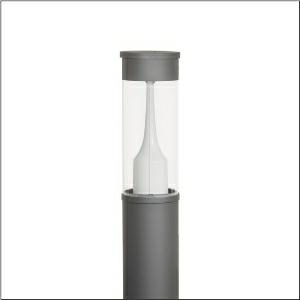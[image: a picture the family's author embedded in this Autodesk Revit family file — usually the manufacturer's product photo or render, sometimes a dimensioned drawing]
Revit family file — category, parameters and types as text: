
# Revit family: city-light_260_iq___st1_2a_5xa5295mf14h_84f0
name_source: partatom
category: Lighting Fixtures
units: mm (PartAtom-declared; Revit-internal decimal feet)

## family parameters
Cut with Voids When Loaded = No
Host = Face
Light Source = No
Part Type = Normal
Room Calculation Point = No
Round Connector Dimension = Use Diameter
Shared = No

## types (1)
- --- (1 x LED, 1540 lm, 11.8 W, 2700K)
    Apparent Load = 12 VA
    CIE Flux Codes = 22 61 93 96 100
    Color Rendering = 70
    Color Temperature = 2700K
    Default Elevation = 1800 mm
    Description = City-Light 260 iQ, light pillar, Module 540 iQ-SR, primary light control with 3 zone facetted reflector, of plastic, silver coated, highly specular, structured, primary optical cover: cover, of PMMA, transparent, partly coated, light distribution: ST1.2a, primary light characteristic: asymmetric, LED, High Power LED, rated luminous flux: 1.540lm, luminous efficacy: 131lm/W, light colour: 727, colour temperature: 2700K, control gear: iQ Street-Remote, control: pre-setting: logarithmic dimming characteristic, Street-Remote, Auto-Match, Temp-Guard, Lumen-Switch, Night-Set, Smart-Wire, Light-Fading, Desk-Remote (wireless, voltage-free reading and setting of iQ features in the workshop via application-optimized NFC function/RFID function), optimised constant luminous flux control (CLO 2.0), with terminal, 6-pole, max. 2.5mm², mains connection: 230..240V, AC, 50/60Hz, start of lifetime: 12W, end of service life: 12W, reduction: 6W, luminaire housing, cylindrical, of extruded aluminium section, coated, Siteco® metallic grey (DB 702S), length: 2.600mm, diameter: 200mm, Module 540 iQ-SR, traffic white (RAL 9016), equipment: standard, protection rating (complete): IP65, insulation class (complete): insulation class II (safety insulation), certification: CE, ENEC, VDE, packaging unit: 1 piece

Light Distribution: ST1.2a
    Height = 500 mm
    Lamp = 1 x LED
    Lamp Light Flux = 1540 lm
    Lamp Power = 11.8 W
    Lamp count = 1
    Length = 200 mm  [stored 0.656168 ft]
    Luminous efficacy = 131 lm/W
    Manufacturer = Siteco
    ModVariant = No
    Model = 5XA5295MF14H
    Mounting Place = Floor
    Mounting Type = Freestanding
    Number of Poles = 1
    OnlyDefault = Yes
    Power Factor = 1
    Product Name = City-Light 260 iQ | ST1.2a
    Product group = light pillar
    ProductGroupID = 1301
    Protection Class = Protection class II
    Protection Degree = IP 65
    RLX_Detail_Level = 1
    RLX_Emergency_Light_Flux = 0 lm
    RLX_Emergency_Type = 0
    RLX_Emergency_Type_DB = No
    RlxData = <blob elided: 60617 chars, md5=fff66f73>
    Socket = socket
    Standby Power = 0 W
    System Light Flux = 1540 lm
    System Power = 12 W
    Type Comments = factory setting: luminous flux: 100 % | dim-lin: 254 | 472 mA
    Type Image = l_1006918.jpg
    URL = http://relux.com
    VarID = @adj_174567
    Voltage = 0 V
    Weight = 0.00 kg
    Width = 0 mm  [stored 0 ft]

note: [stored X ft] marks values corroborated as IEEE doubles in the binary element streams (Revit-internal decimal feet)

## geometry (parser evidence)
native form markers: Blend x4, Sweep x11
no freeform markers — native parametric forms only
